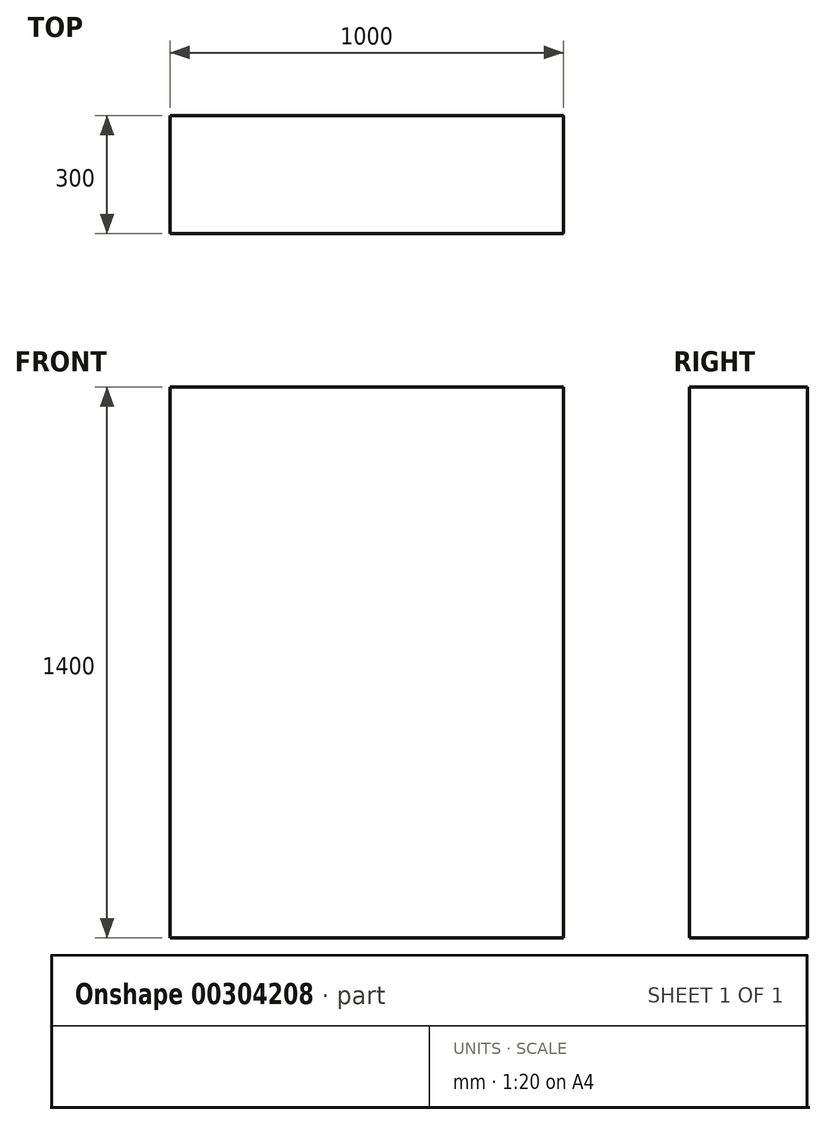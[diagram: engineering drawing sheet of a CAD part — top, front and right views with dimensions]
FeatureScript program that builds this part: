
annotation { "Feature Type Name" : "Feature", "Feature Type Description" : "" }
export const myFeature = defineFeature(function(context is Context, id is Id, definition is map)
    precondition{}
    {
        {
            var Q0;
            Q0=qCreatedBy(makeId("Front.planeOp"),FACE);
            var sketch = newSketch(context, id + "F0", { "sketchPlane" : qUnion([Q0])});
            skLineSegment(sketch, "E0.bottom", {"start": v(0, 1400) * mm, "end": v(1000, 1400) * mm});
            skLineSegment(sketch, "E0.top", {"start": v(0, 0) * mm, "end": v(1000, 0) * mm});
            skLineSegment(sketch, "E0.left", {"start": v(0, 1400) * mm, "end": v(0, 0) * mm});
            skLineSegment(sketch, "E0.right", {"start": v(1000, 1400) * mm, "end": v(1000, 0) * mm});
            skSolve(sketch);
        }
        {
            var Q0;
            Q0 = qSketchRegion(id + "F0", true);
            extrude(context, id + "F1", {"entities" : qUnion([Q0]), "depth" : 300 * mm});
        }
    });
